# Revit family: DA_Клапан_постоянного_расхода воздуха_RPM_VEOX
name_source: partatom
category: Арматура воздуховодов
units: mm (PartAtom-declared; Revit-internal decimal feet)

## family parameters
Всегда вертикально = Да
На основе рабочей плоскости = Нет
Общий = Нет
При загрузке вырезать с полостями = Нет
Размер круглого соединителя = Использовать диаметр
Тип детали = Вставляется

## types (1)
- RPM 3-6.5 м/с
    ADSK_Количество = 1
    Drive visibility = Да
    Drive visibility-Z = Нет
    Flap visbility 1 = Нет
    Insulation = Rock wool
    Insulation filter = Z
    Insulation visibility = Нет
    Metal plate = Galvanized steel
    Mode = P
    Seal = Plastic
    Длина = 385 мм
    КМС = 5.5
    ОБЩ_Владелец вида = RPM
    ОБЩ_ДатаСемейства = 20240304
    ОБЩ_Единица измерения = шт
    ОБЩ_Завод-изготовитель = Veox
    ОБЩ_Наименование краткое = РРДРП
    ОБЩ_Обозначение = RPM
    вылет шумоизол = 1 мм
    изоляция выбор = 0

## geometry (parser evidence)
native form markers: Blend x2, Sweep x5
no freeform markers — native parametric forms only
